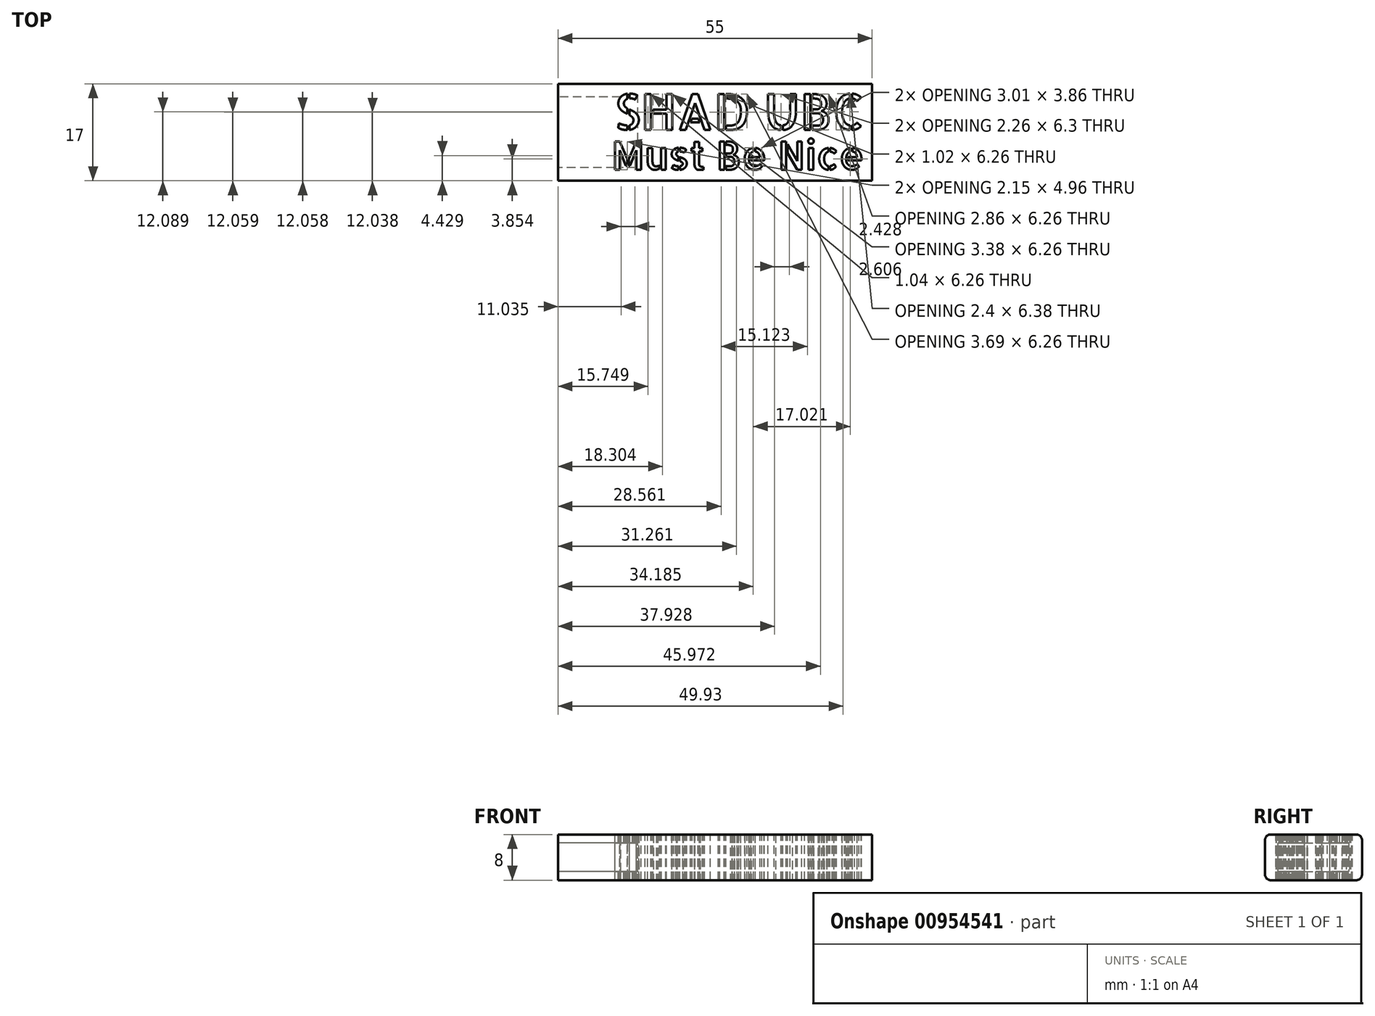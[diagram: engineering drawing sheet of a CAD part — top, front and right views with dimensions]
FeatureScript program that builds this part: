
annotation { "Feature Type Name" : "Feature", "Feature Type Description" : "" }
export const myFeature = defineFeature(function(context is Context, id is Id, definition is map)
    precondition{}
    {
        {
            var Q0;
            Q0=qCreatedBy(makeId("Front.planeOp"),FACE);
            var sketch = newSketch(context, id + "F0", { "sketchPlane" : qUnion([Q0])});
            skLineSegment(sketch, "E0.bottom", {"start": v(-7.5, 4) * mm, "end": v(7.5, 4) * mm});
            skLineSegment(sketch, "E0.top", {"start": v(-7.5, -4) * mm, "end": v(7.5, -4) * mm});
            skLineSegment(sketch, "E0.left", {"start": v(-8.5, 3) * mm, "end": v(-8.5, -3) * mm});
            skLineSegment(sketch, "E0.right", {"start": v(8.5, 3) * mm, "end": v(8.5, -3) * mm});
            skPoint(sketch, "E0.middle", {"position": v(0, 0) * mm});
            skPoint(sketch, "E1.visualSharp", {"position": v(-8.5, 4) * mm});
            skArc(sketch, "E1.filletArc", {"start": v(-7.5, 4) * mm, "mid": v(-8.2, 3.7) * mm, "end": v(-8.5, 3) * mm});
            skPoint(sketch, "E2.visualSharp", {"position": v(-8.5, -4) * mm});
            skArc(sketch, "E2.filletArc", {"start": v(-8.5, -3) * mm, "mid": v(-8.2, -3.7) * mm, "end": v(-7.5, -4) * mm});
            skPoint(sketch, "E3.visualSharp", {"position": v(8.5, -4) * mm});
            skArc(sketch, "E3.filletArc", {"start": v(7.5, -4) * mm, "mid": v(8.2, -3.7) * mm, "end": v(8.5, -3) * mm});
            skPoint(sketch, "E4.visualSharp", {"position": v(8.5, 4) * mm});
            skArc(sketch, "E4.filletArc", {"start": v(8.5, 3) * mm, "mid": v(8.2, 3.7) * mm, "end": v(7.5, 4) * mm});
            skSolve(sketch);
        }
        {
            var Q0;
            Q0 = qSketchRegion(id + "F0", true);
            extrude(context, id + "F1", {"entities" : qUnion([Q0]), "depth" : 55 * mm, "offsetDistance" : 25 * mm});
        }
        {
            var Q0;
            Q0=makeQuery(id+"F1.opExtrude","CAP_FACE",FACE,{"disambiguationData":[OSD([sQuery(id+"F0.wireOp",EDGE,"E0.bottom"),sQuery(id+"F0.wireOp",EDGE,"E0.top"),sQuery(id+"F0.wireOp",EDGE,"E0.left"),sQuery(id+"F0.wireOp",EDGE,"E0.right"),sQuery(id+"F0.wireOp",EDGE,"E1.filletArc"),sQuery(id+"F0.wireOp",EDGE,"E2.filletArc"),sQuery(id+"F0.wireOp",EDGE,"E3.filletArc"),sQuery(id+"F0.wireOp",EDGE,"E4.filletArc")])],"isStart":false});
            var sketch = newSketch(context, id + "F2", { "sketchPlane" : qUnion([Q0])});
            skLineSegment(sketch, "E5.bottom", {"start": v(6.2, -2.5) * mm, "end": v(-6.2, -2.5) * mm});
            skLineSegment(sketch, "E5.top", {"start": v(6.2, 2.5) * mm, "end": v(-6.2, 2.5) * mm});
            skLineSegment(sketch, "E5.left", {"start": v(6.2, -2.5) * mm, "end": v(6.2, 2.5) * mm});
            skLineSegment(sketch, "E5.right", {"start": v(-6.2, -2.5) * mm, "end": v(-6.2, 2.5) * mm});
            skPoint(sketch, "E5.middle", {"position": v(0, 0) * mm});
            skSolve(sketch);
        }
        {
            var Q0;
            Q0=makeQuery(id+"F2.imprint","IMPRINT",FACE,{"disambiguationData":[TD([[makeQuery(id+"F2.imprint","IMPRINT",EDGE,{"derivedFrom":sQuery(id+"F2.wireOp",EDGE,"E5.bottom")}),-1.0]])]});
            extrude(context, id + "F3", {"entities" : qUnion([Q0]), "operationType" : NewBodyOperationType.REMOVE, "oppositeDirection" : true, "depth" : 14 * mm, "offsetDistance" : 25 * mm});
        }
        {
            var Q0;
            Q0=makeQuery(id+"F1.opExtrude","SWEPT_BODY",BODY,{"disambiguationData":[OSD([sQuery(id+"F0.wireOp",EDGE,"E0.bottom"),sQuery(id+"F0.wireOp",EDGE,"E0.top"),sQuery(id+"F0.wireOp",EDGE,"E0.left"),sQuery(id+"F0.wireOp",EDGE,"E0.right"),sQuery(id+"F0.wireOp",EDGE,"E1.filletArc"),sQuery(id+"F0.wireOp",EDGE,"E2.filletArc"),sQuery(id+"F0.wireOp",EDGE,"E3.filletArc"),sQuery(id+"F0.wireOp",EDGE,"E4.filletArc")])]});
            var Q1;
            Q1=makeQuery(id+"F1.opExtrude","CAP_EDGE",EDGE,{"disambiguationData":[OSD([sQuery(id+"F0.wireOp",EDGE,"E0.right")])],"isStart":false});
            transform(context, id + "F4", {"entities" : qUnion([Q0]), "transformType" : TransformType.ROTATION, "transformAxis" : qUnion([Q1]), "angle" : 90 * degree, "makeCopy" : false});
        }
        {
            var Q0;
            Q0=makeQuery(id+"F1.opExtrude","SWEPT_FACE",FACE,{"disambiguationData":[OSD([sQuery(id+"F0.wireOp",EDGE,"E0.bottom")])]});
            var sketch = newSketch(context, id + "F5", { "sketchPlane" : qUnion([Q0])});
            skPoint(sketch, "E6.secondSnap0", {"position": v(63.5, -46.5) * mm});
            skText(sketch, "E7", { "text": "SHAD UBC", "fontName": "AllertaStencil-Regular.ttf"});
            const initialGuessF5  = {"E7": [0.01833, -0.04607, 1, 0, 0.00626]};
            skSetInitialGuess(sketch, initialGuessF5);
            skSolve(sketch);
        }
        {
            var Q0;
            Q0 = qSketchRegion(id + "F5", true);
            extrude(context, id + "F6", {"entities" : qUnion([Q0]), "operationType" : NewBodyOperationType.REMOVE, "oppositeDirection" : true, "depth" : 10 * mm, "offsetDistance" : 25 * mm});
        }
        {
            var Q0;
            Q0=makeQuery(id+"F1.opExtrude","SWEPT_FACE",FACE,{"disambiguationData":[OSD([sQuery(id+"F0.wireOp",EDGE,"E0.bottom")])]});
            var sketch = newSketch(context, id + "F7", { "sketchPlane" : qUnion([Q0])});
            skText(sketch, "E8", { "text": "Must Be Nice", "fontName": "AllertaStencil-Regular.ttf"});
            const initialGuessF7  = {"E8": [0.01784, -0.05305, 1, 0, 0.00496]};
            skSetInitialGuess(sketch, initialGuessF7);
            skSolve(sketch);
        }
        {
            var Q0;
            Q0 = qSketchRegion(id + "F7", true);
            extrude(context, id + "F8", {"entities" : qUnion([Q0]), "operationType" : NewBodyOperationType.REMOVE, "oppositeDirection" : true, "depth" : 10 * mm, "offsetDistance" : 25 * mm});
        }
    });
